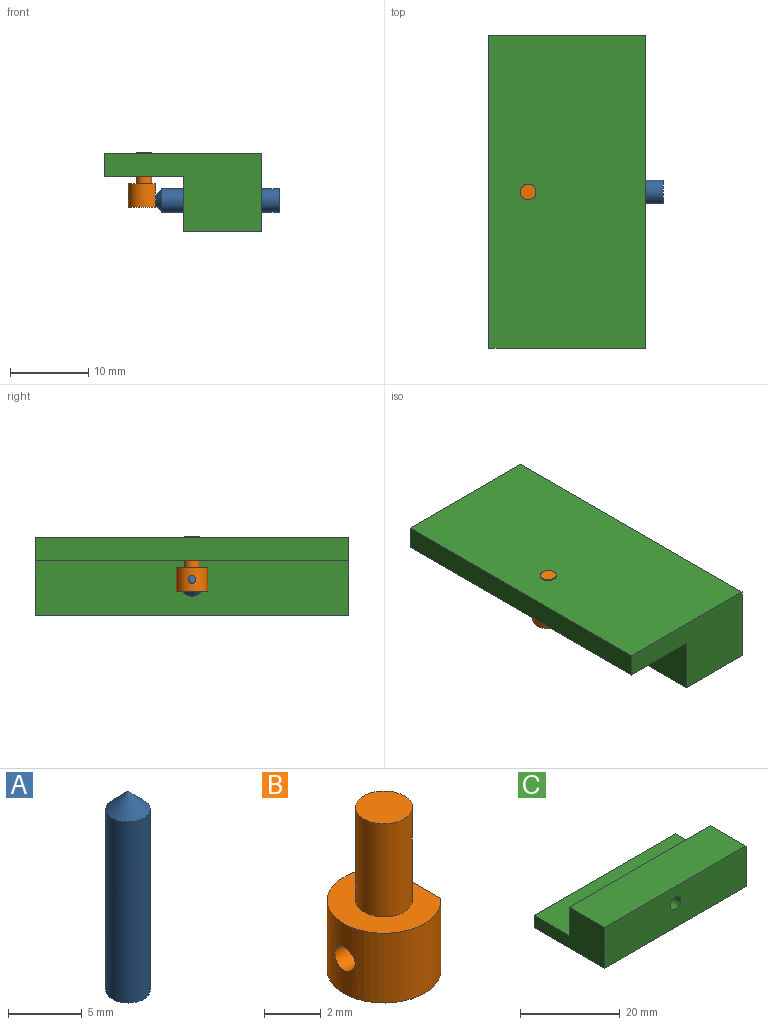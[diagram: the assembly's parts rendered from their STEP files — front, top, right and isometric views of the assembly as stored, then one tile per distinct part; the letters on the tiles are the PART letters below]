
ASSEMBLY  parts=3 mates=3
PART A: 3 faces, bbox 3x3x16.5 mm
  f0: cylinder r=1.5mm len=15mm, axis (0,0,-1), area 141.4mm2, adj f1,f2
  f1: plane 3x3mm, normal (0,0,-1), area 7.1mm2, adj f0
  f2: cone r=0mm half-angle=45deg, axis (0,0,-1), area 10mm2, adj f0
PART B: 9 faces, bbox 3.5x4x7 mm
  f0: cylinder r=2mm len=4mm, axis (0,0,1), area 28.1mm2, adj f1,f2,f5,f6,f7,f8
  f1: plane 4x3.5mm, normal (0,0,-1), area 11.7mm2, adj f0,f7
  f2: plane 4x3.5mm, normal (0,0,1), area 8.5mm2, adj f0,f3,f8
  f3: cylinder r=1mm len=4mm, axis (0,0,-1), area 25.1mm2, adj f2,f4
  f4: plane 2x2mm, normal (0,0,1), area 3.1mm2, adj f3
  f5: cylinder r=0.5mm len=2.55mm, axis (1,0,0), area 7.9mm2, adj f0,f6
  f6: cone r=0.5mm half-angle=45deg, axis (1,0,0), area 8.1mm2, adj f0,f5,f7,f8
  f7: plane 2.65x0.91mm, normal (1,0,0), area 0.8mm2, adj f0,f1,f6
  f8: plane 2.65x0.91mm, normal (1,0,0), area 0.8mm2, adj f0,f2,f6
PART C: 10 faces, bbox 40x20x10 mm
  f0: plane 20x10mm, normal (-1,0,0), area 130mm2, adj f2,f3,f4,f5,f6,f7
  f1: plane 20x10mm, normal (1,0,0), area 130mm2, adj f2,f3,f4,f5,f6,f7
  f2: plane 40x3mm, normal (0,1,0), area 120mm2, adj f0,f1,f5,f7
  f3: plane 40x10mm, normal (0,-1,0), area 392.9mm2, adj f0,f1,f4,f5,f8
  f4: plane 40x10mm, normal (0,0,1), area 400mm2, adj f0,f1,f3,f6
  f5: plane 40x20mm, normal (0,0,-1), area 796.9mm2, adj f0,f1,f2,f3,f9
  f6: plane 40x7mm, normal (0,1,0), area 272.9mm2, adj f0,f1,f4,f7,f8
  f7: plane 40x10mm, normal (0,0,1), area 396.9mm2, adj f0,f1,f2,f6,f9
  f8: cylinder r=1.5mm len=10mm, axis (0,-1,0), area 94.2mm2, adj f3,f6
  f9: cylinder r=1mm len=3mm, axis (0,0,1), area 18.8mm2, adj f5,f7
PLACE A rot(axis=(0.58,-0.58,-0.58),120deg) t=(8.07,5.65,11.87)mm
PLACE B t=(-9.17,5.65,14.01)mm
PLACE C rot(axis=(0.71,-0.71,0),180deg) t=(-4.17,5.65,17.87)mm fixed
MATE parallel B.f8 <-> C.f6  axis (1,0,0) through (-7.67,5.65,13.77)mm
MATE cylindrical C.f9 <-> B.f0  axis (0,0,-1) through (-9.17,5.65,14.87)mm
MATE slider A.f0 <-> C.f8  axis (1,0,0) through (0.57,5.65,11.87)mm
